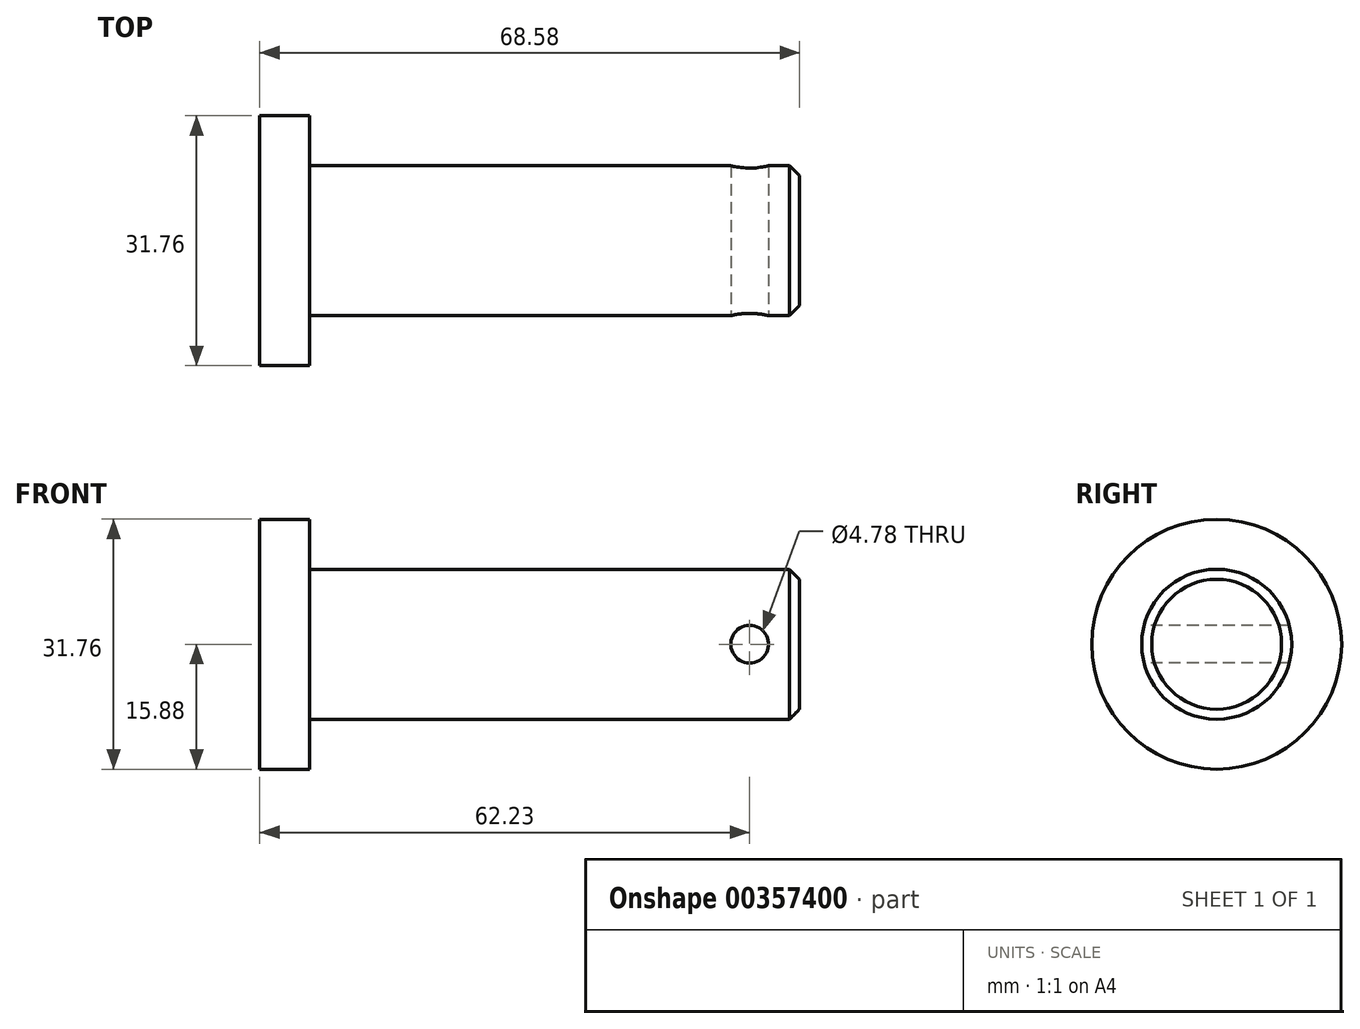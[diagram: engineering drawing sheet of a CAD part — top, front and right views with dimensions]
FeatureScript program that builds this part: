
annotation { "Feature Type Name" : "Feature", "Feature Type Description" : "" }
export const myFeature = defineFeature(function(context is Context, id is Id, definition is map)
    precondition{}
    {
        {
            var Q0;
            Q0=qCreatedBy(makeId("Right.planeOp"),FACE);
            var sketch = newSketch(context, id + "F0", { "sketchPlane" : qUnion([Q0])});
            skCircle(sketch, "E0", {"center": v(0, 0) * mm, "radius": 15.88 * mm});
            skSolve(sketch);
        }
        {
            var Q0;
            Q0 = qSketchRegion(id + "F0", true);
            extrude(context, id + "F1", {"entities" : qUnion([Q0]), "depth" : 6.35 * mm});
        }
        {
            var Q0;
            Q0=makeQuery(id+"F1.opExtrude","CAP_FACE",FACE,{"disambiguationData":[OSD([sQuery(id+"F0.wireOp",EDGE,"E0")])],"isStart":false});
            var sketch = newSketch(context, id + "F2", { "sketchPlane" : qUnion([Q0])});
            skCircle(sketch, "E1", {"center": v(0, 0) * mm, "radius": 9.53 * mm});
            skSolve(sketch);
        }
        {
            var Q0;
            Q0 = qSketchRegion(id + "F2", true);
            extrude(context, id + "F3", {"entities" : qUnion([Q0]), "operationType" : NewBodyOperationType.ADD, "depth" : 62.23 * mm});
        }
        {
            var Q0;
            Q0=makeQuery(id+"F3.opExtrude","CAP_EDGE",EDGE,{"disambiguationData":[OSD([sQuery(id+"F2.wireOp",EDGE,"E1")])],"isStart":false});
            chamfer(context, id + "F4", {"entities" : qUnion([Q0]), "width" : 1.27 * mm, "tangentPropagation" : true});
        }
        {
            var Q0;
            Q0=qCreatedBy(makeId("Front.planeOp"),FACE);
            var sketch = newSketch(context, id + "F5", { "sketchPlane" : qUnion([Q0])});
            skCircle(sketch, "E2", {"center": v(62.23, 0) * mm, "radius": 2.39 * mm});
            skSolve(sketch);
        }
        {
            var Q0;
            Q0 = qSketchRegion(id + "F5", true);
            extrude(context, id + "F6", {"entities" : qUnion([Q0]), "operationType" : NewBodyOperationType.REMOVE, "endBound" : BoundingType.THROUGH_ALL, "oppositeDirection" : true, "depth" : 25.4 * mm});
        }
        {
            var Q0;
            Q0=makeQuery(id+"F6.boolean.opBoolean","COPY",FACE,{"derivedFrom":makeQuery(id+"F6.opExtrude","CAP_FACE",FACE,{"disambiguationData":[OSD([sQuery(id+"F5.wireOp",EDGE,"E2")])],"isStart":true})});
            var sketch = newSketch(context, id + "F7", { "sketchPlane" : qUnion([Q0])});
            skCircle(sketch, "E3", {"center": v(-62.23, 0) * mm, "radius": 2.39 * mm});
            skSolve(sketch);
        }
        {
            var Q0;
            Q0 = qSketchRegion(id + "F7", true);
            extrude(context, id + "F8", {"entities" : qUnion([Q0]), "operationType" : NewBodyOperationType.REMOVE, "endBound" : BoundingType.THROUGH_ALL, "oppositeDirection" : true, "depth" : 25.4 * mm});
        }
    });
